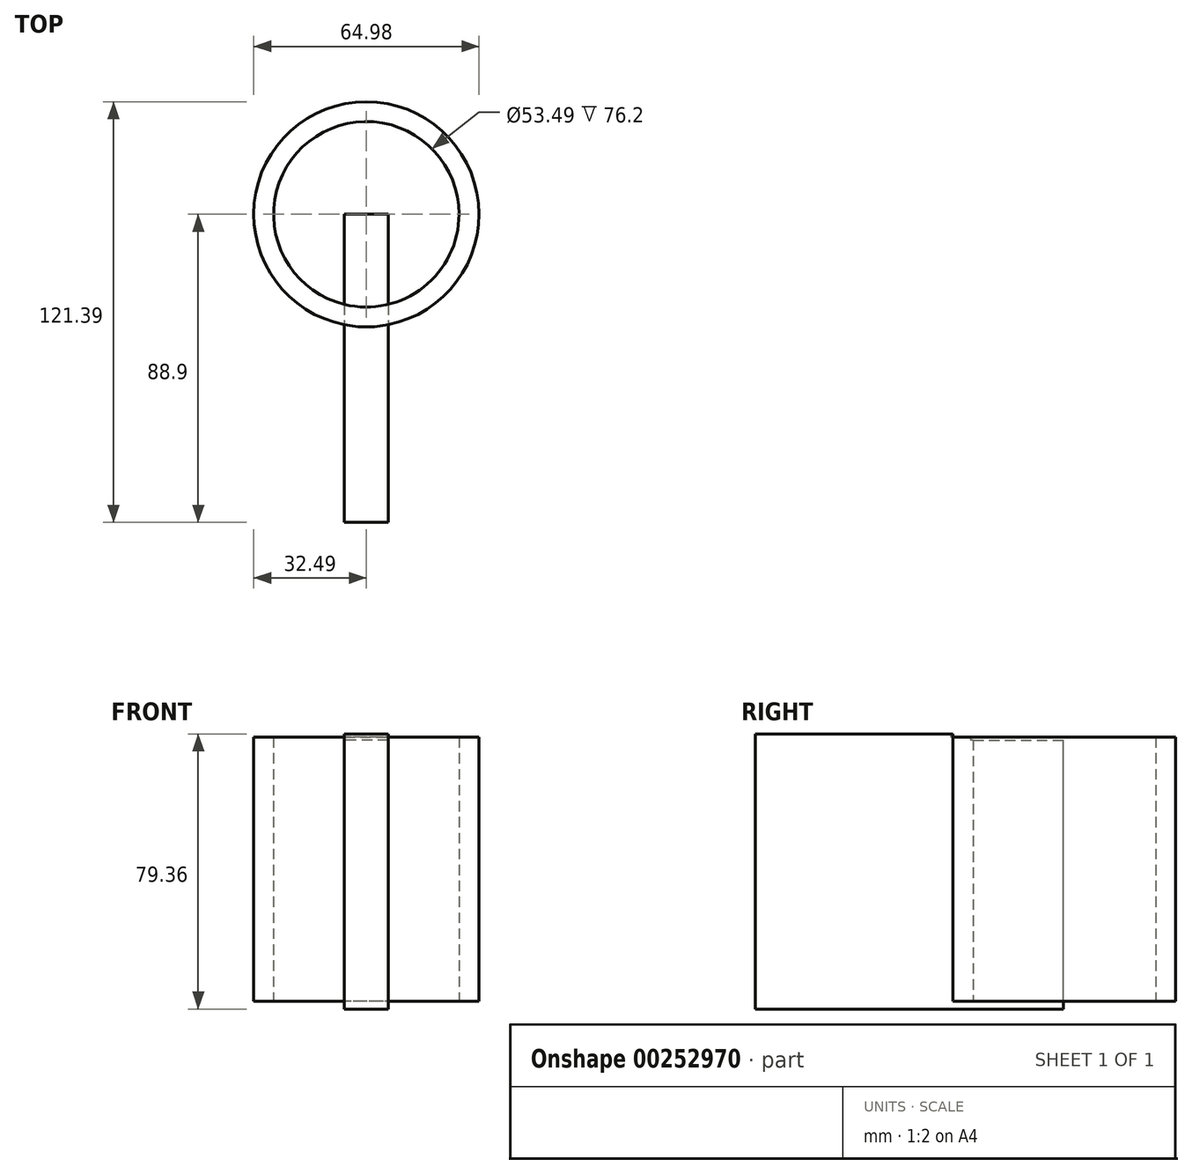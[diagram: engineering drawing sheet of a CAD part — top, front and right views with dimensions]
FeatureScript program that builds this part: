
annotation { "Feature Type Name" : "Feature", "Feature Type Description" : "" }
export const myFeature = defineFeature(function(context is Context, id is Id, definition is map)
    precondition{}
    {
        {
            var Q0;
            Q0=qCreatedBy(makeId("Top.planeOp"),FACE);
            var sketch = newSketch(context, id + "F0", { "sketchPlane" : qUnion([Q0])});
            skCircle(sketch, "E0", {"center": v(0, 0) * mm, "radius": 32.49 * mm});
            skCircle(sketch, "E1", {"center": v(0, 0) * mm, "radius": 26.75 * mm});
            skSolve(sketch);
        }
        {
            var Q0;
            Q0=makeQuery(id+"F0.imprint","IMPRINT",FACE,{"disambiguationData":[TD([[makeQuery(id+"F0.imprint","IMPRINT",EDGE,{"derivedFrom":sQuery(id+"F0.wireOp",EDGE,"E0")}),1.0]])]});
            extrude(context, id + "F1", {"entities" : qUnion([Q0]), "depth" : 50.8 * mm});
        }
        {
            var Q0;
            Q0=makeQuery(id+"F1.opExtrude","CAP_FACE",FACE,{"disambiguationData":[OSD([sQuery(id+"F0.wireOp",EDGE,"E0"),sQuery(id+"F0.wireOp",EDGE,"E1")])],"isStart":true});
            extrude(context, id + "F2", {"entities" : qUnion([Q0]), "operationType" : NewBodyOperationType.ADD, "depth" : 25.4 * mm});
        }
        {
            var Q0;
            Q0=qCreatedBy(makeId("Front.planeOp"),FACE);
            var sketch = newSketch(context, id + "F3", { "sketchPlane" : qUnion([Q0])});
            skLineSegment(sketch, "E2.bottom", {"start": v(6.32, -27.6) * mm, "end": v(-6.32, -27.6) * mm});
            skLineSegment(sketch, "E2.top", {"start": v(6.32, 49.98) * mm, "end": v(-6.32, 49.98) * mm});
            skLineSegment(sketch, "E2.left", {"start": v(6.32, -27.6) * mm, "end": v(6.32, 49.98) * mm});
            skLineSegment(sketch, "E2.right", {"start": v(-6.32, -27.6) * mm, "end": v(-6.32, 49.98) * mm});
            skPoint(sketch, "E2.middle", {"position": v(0, 11.19) * mm});
            skSolve(sketch);
        }
        {
            var Q0;
            Q0=makeQuery(id+"F3.imprint","IMPRINT",FACE,{"disambiguationData":[TD([[makeQuery(id+"F3.imprint","IMPRINT",EDGE,{"derivedFrom":sQuery(id+"F3.wireOp",EDGE,"E2.bottom")}),-1.0]])]});
            extrude(context, id + "F4", {"entities" : qUnion([Q0]), "operationType" : NewBodyOperationType.ADD, "depth" : 88.9 * mm});
        }
        {
            var Q0;
            {var subQ2=sQuery(id+"F3.wireOp",EDGE,"E2.top");var subQ3=sQuery(id+"F0.wireOp",EDGE,"E0");Q0=makeQuery(id+"F4.boolean.opBoolean","SPLIT",FACE,{"disambiguationData":[TD([makeQuery(id+"F1.opExtrude","SWEPT_FACE",FACE,{"disambiguationData":[OSD([subQ3])]})])],"derivedFrom":makeQuery(id+"F4.opExtrude","SWEPT_FACE",FACE,{"disambiguationData":[OSD([subQ2])]})});}
            extrude(context, id + "F5", {"entities" : qUnion([Q0]), "operationType" : NewBodyOperationType.ADD, "depth" : 1.77 * mm});
        }
    });
